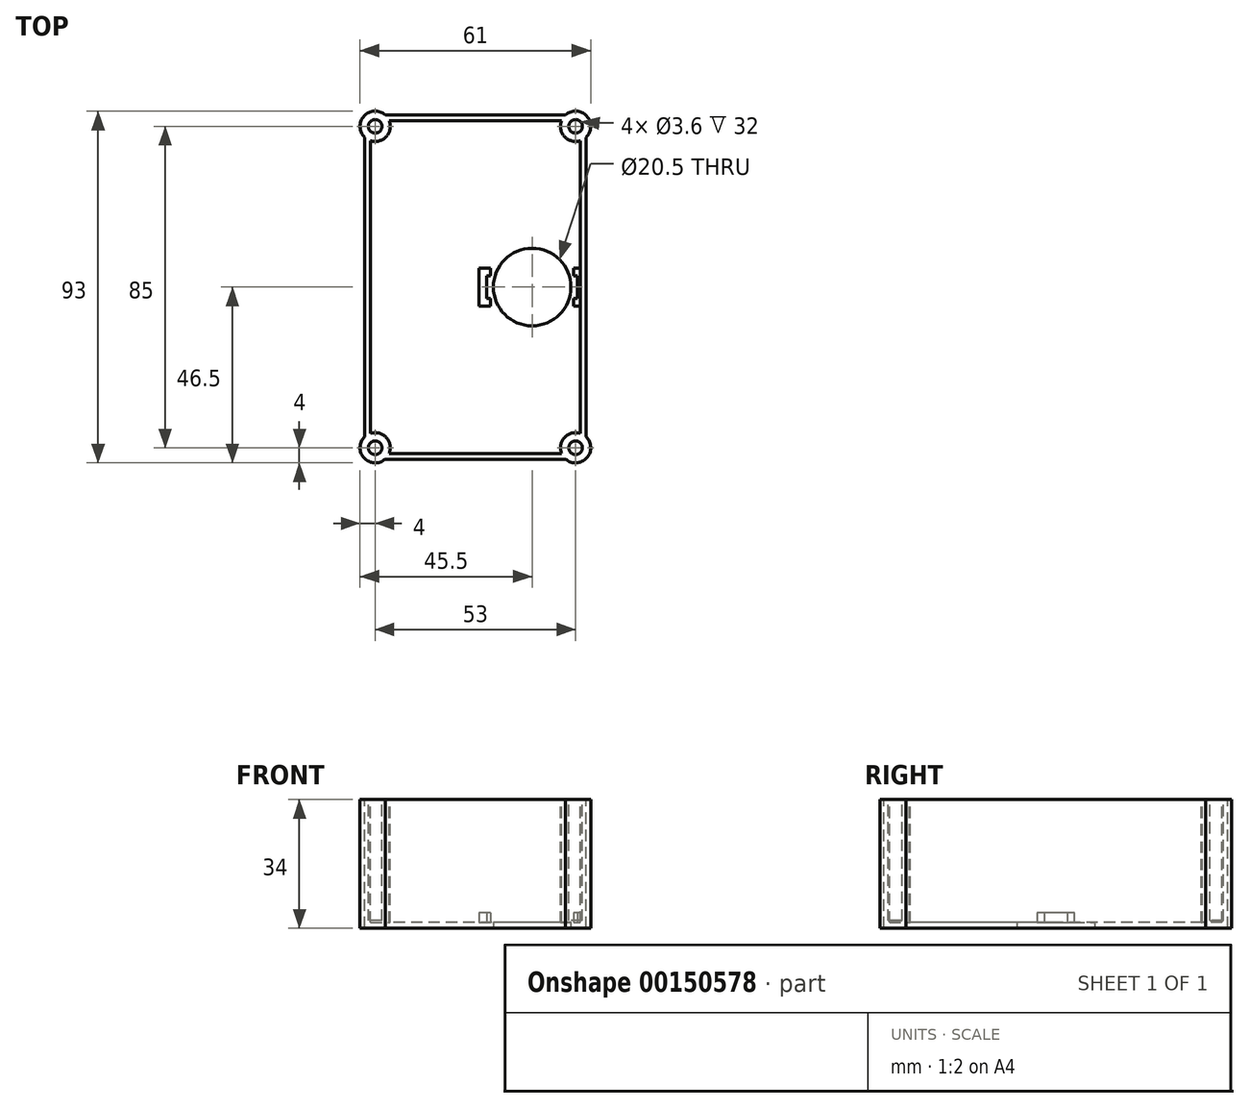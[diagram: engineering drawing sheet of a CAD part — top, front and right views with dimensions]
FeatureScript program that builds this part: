
annotation { "Feature Type Name" : "Feature", "Feature Type Description" : "" }
export const myFeature = defineFeature(function(context is Context, id is Id, definition is map)
    precondition{}
    {
        {
            var Q0;
            Q0=qCreatedBy(makeId("Top.planeOp"),FACE);
            var sketch = newSketch(context, id + "F0", { "sketchPlane" : qUnion([Q0])});
            skLineSegment(sketch, "E0.bottom", {"start": v(29.25, 45.5) * mm, "end": v(-29.25, 45.5) * mm});
            skLineSegment(sketch, "E0.top", {"start": v(29.25, -45.5) * mm, "end": v(-29.25, -45.5) * mm});
            skLineSegment(sketch, "E0.left", {"start": v(29.25, 45.5) * mm, "end": v(29.25, -45.5) * mm});
            skLineSegment(sketch, "E0.right", {"start": v(-29.25, 45.5) * mm, "end": v(-29.25, -45.5) * mm});
            skPoint(sketch, "E0.middle", {"position": v(0, 0) * mm});
            skSolve(sketch);
        }
        {
            var Q0;
            Q0=qSketchRegion(id+"F0",true);
            extrude(context, id + "F1", {"entities" : qUnion([Q0]), "oppositeDirection" : true, "depth" : 34 * mm});
        }
        {
            var Q0;
            Q0=makeQuery(id+"F1.opExtrude","CAP_FACE",FACE,{"disambiguationData":[OSD([sQuery(id+"F0.wireOp",EDGE,"E0.bottom"),sQuery(id+"F0.wireOp",EDGE,"E0.top"),sQuery(id+"F0.wireOp",EDGE,"E0.left"),sQuery(id+"F0.wireOp",EDGE,"E0.right")])],"isStart":true});
            shell(context, id + "F2", {"entities" : qUnion([Q0]), "thickness" : 1.5 * mm});
        }
        {
            var Q0;
            Q0=makeQuery(id+"F1.opExtrude","SWEPT_EDGE",EDGE,{"disambiguationData":[OSD([sQuery(id+"F0.wireOp",EDGE,"E0.bottom"),sQuery(id+"F0.wireOp",EDGE,"E0.right")])]});
            var Q1;
            Q1=makeQuery(id+"F1.opExtrude","SWEPT_EDGE",EDGE,{"disambiguationData":[OSD([sQuery(id+"F0.wireOp",EDGE,"E0.bottom"),sQuery(id+"F0.wireOp",EDGE,"E0.left")])]});
            var Q2;
            Q2=makeQuery(id+"F1.opExtrude","SWEPT_EDGE",EDGE,{"disambiguationData":[OSD([sQuery(id+"F0.wireOp",EDGE,"E0.top"),sQuery(id+"F0.wireOp",EDGE,"E0.right")])]});
            var Q3;
            Q3=makeQuery(id+"F1.opExtrude","SWEPT_EDGE",EDGE,{"disambiguationData":[OSD([sQuery(id+"F0.wireOp",EDGE,"E0.top"),sQuery(id+"F0.wireOp",EDGE,"E0.left")])]});
            fillet(context, id + "F3", {"entities" : qUnion([Q0, Q1, Q2, Q3]), "radius" : 3 * mm, "tangentPropagation" : true, "allowEdgeOverflow" : false});
        }
        {
            var Q0;
            Q0=makeQuery(id+"F2.opShell","OFFSET_EDGE",EDGE,{"disambiguationData":[OSD([sQuery(id+"F0.wireOp",EDGE,"E0.bottom"),sQuery(id+"F0.wireOp",EDGE,"E0.right")])]});
            var Q1;
            Q1=makeQuery(id+"F2.opShell","OFFSET_EDGE",EDGE,{"disambiguationData":[OSD([sQuery(id+"F0.wireOp",EDGE,"E0.top"),sQuery(id+"F0.wireOp",EDGE,"E0.right")])]});
            var Q2;
            Q2=makeQuery(id+"F2.opShell","OFFSET_EDGE",EDGE,{"disambiguationData":[OSD([sQuery(id+"F0.wireOp",EDGE,"E0.top"),sQuery(id+"F0.wireOp",EDGE,"E0.left")])]});
            var Q3;
            Q3=makeQuery(id+"F2.opShell","OFFSET_EDGE",EDGE,{"disambiguationData":[OSD([sQuery(id+"F0.wireOp",EDGE,"E0.bottom"),sQuery(id+"F0.wireOp",EDGE,"E0.left")])]});
            fillet(context, id + "F4", {"entities" : qUnion([Q0, Q1, Q2, Q3]), "radius" : 2 * mm, "tangentPropagation" : true, "allowEdgeOverflow" : false});
        }
        {
            var Q0;
            Q0=makeQuery(id+"F0.imprint","IMPRINT",FACE,{"disambiguationData":[TD([[makeQuery(id+"F0.imprint","IMPRINT",EDGE,{"derivedFrom":sQuery(id+"F0.wireOp",EDGE,"E0.bottom")}),1.0]])]});
            var sketch = newSketch(context, id + "F5", { "sketchPlane" : qUnion([Q0])});
            skLineSegment(sketch, "E1", {"start": v(26.5, -42.5) * mm, "end": v(26.5, 42.5) * mm, "construction": true});
            skLineSegment(sketch, "E2", {"start": v(-26.5, 42.5) * mm, "end": v(-26.5, -42.5) * mm, "construction": true});
            skLineSegment(sketch, "E3", {"start": v(26.5, -42.5) * mm, "end": v(-26.5, -42.5) * mm, "construction": true});
            skLineSegment(sketch, "E4", {"start": v(26.5, 42.5) * mm, "end": v(-26.5, 42.5) * mm, "construction": true});
            skCircle(sketch, "E5", {"center": v(26.5, -42.5) * mm, "radius": 4 * mm});
            skCircle(sketch, "E6", {"center": v(26.5, 42.5) * mm, "radius": 4 * mm});
            skCircle(sketch, "E7", {"center": v(-26.5, 42.5) * mm, "radius": 4 * mm});
            skCircle(sketch, "E8", {"center": v(-26.5, -42.5) * mm, "radius": 4 * mm});
            skSolve(sketch);
        }
        {
            var Q0;
            Q0=qSketchRegion(id+"F5",true);
            extrude(context, id + "F6", {"entities" : qUnion([Q0]), "operationType" : NewBodyOperationType.ADD, "oppositeDirection" : true, "depth" : 34 * mm});
        }
        {
            var Q0;
            Q0=qCreatedBy(makeId("Top.planeOp"),FACE);
            var sketch = newSketch(context, id + "F7", { "sketchPlane" : qUnion([Q0])});
            skCircle(sketch, "E9", {"center": v(26.5, -42.5) * mm, "radius": 1.8 * mm});
            skCircle(sketch, "E10", {"center": v(26.5, 42.5) * mm, "radius": 1.8 * mm});
            skCircle(sketch, "E11", {"center": v(-26.5, -42.5) * mm, "radius": 1.8 * mm});
            skCircle(sketch, "E12", {"center": v(-26.5, 42.5) * mm, "radius": 1.8 * mm});
            skSolve(sketch);
        }
        {
            var Q0;
            Q0=qSketchRegion(id+"F7",true);
            extrude(context, id + "F8", {"entities" : qUnion([Q0]), "operationType" : NewBodyOperationType.REMOVE, "oppositeDirection" : true, "depth" : 32 * mm});
        }
        {
            var Q0;
            Q0=makeQuery(id+"F0.imprint","IMPRINT",FACE,{"disambiguationData":[TD([[makeQuery(id+"F0.imprint","IMPRINT",EDGE,{"derivedFrom":sQuery(id+"F0.wireOp",EDGE,"E0.bottom")}),1.0]])]});
            var sketch = newSketch(context, id + "F9", { "sketchPlane" : qUnion([Q0])});
            skArc(sketch, "E13", {"start": v(27.75, -37.9) * mm, "mid": v(21.78, -38.03) * mm, "end": v(21.9, -44) * mm, "construction": true});
            skArc(sketch, "E14", {"start": v(21.9, 44) * mm, "mid": v(21.78, 38.03) * mm, "end": v(27.75, 37.9) * mm, "construction": true});
            skArc(sketch, "E15", {"start": v(-25.85, 35.82) * mm, "mid": v(-19.79, 37.94) * mm, "end": v(-21.9, 44) * mm, "construction": true});
            skArc(sketch, "E16", {"start": v(-21.9, -44) * mm, "mid": v(-22.32, -40.44) * mm, "end": v(-25.85, -39.82) * mm, "construction": true});
            skLineSegment(sketch, "E17", {"start": v(-25.85, -39.82) * mm, "end": v(-25.85, 35.82) * mm, "construction": true});
            skLineSegment(sketch, "E18", {"start": v(-21.9, 44) * mm, "end": v(21.9, 44) * mm, "construction": true});
            skLineSegment(sketch, "E19", {"start": v(27.75, -37.9) * mm, "end": v(27.75, 37.9) * mm, "construction": true});
            skLineSegment(sketch, "E20", {"start": v(21.9, -44) * mm, "end": v(-21.9, -44) * mm, "construction": true});
            skSolve(sketch);
        }
        {
            var Q0;
            Q0=makeQuery(id+"F6.boolean.opBoolean","MERGE",FACE,{"derivedFrom":[makeQuery(id+"F1.opExtrude","CAP_FACE",FACE,{"disambiguationData":[OSD([sQuery(id+"F0.wireOp",EDGE,"E0.bottom"),sQuery(id+"F0.wireOp",EDGE,"E0.top"),sQuery(id+"F0.wireOp",EDGE,"E0.left"),sQuery(id+"F0.wireOp",EDGE,"E0.right")])],"isStart":false}),makeQuery(id+"F6.opExtrude","CAP_FACE",FACE,{"disambiguationData":[OSD([sQuery(id+"F5.wireOp",EDGE,"E5")])],"isStart":false}),makeQuery(id+"F6.opExtrude","CAP_FACE",FACE,{"disambiguationData":[OSD([sQuery(id+"F5.wireOp",EDGE,"E6")])],"isStart":false}),makeQuery(id+"F6.opExtrude","CAP_FACE",FACE,{"disambiguationData":[OSD([sQuery(id+"F5.wireOp",EDGE,"E7")])],"isStart":false}),makeQuery(id+"F6.opExtrude","CAP_FACE",FACE,{"disambiguationData":[OSD([sQuery(id+"F5.wireOp",EDGE,"E8")])],"isStart":false})]});
            var sketch = newSketch(context, id + "F10", { "sketchPlane" : qUnion([Q0])});
            skLineSegment(sketch, "E21", {"start": v(0, 0) * mm, "end": v(15, 0) * mm, "construction": true});
            skCircle(sketch, "E22", {"center": v(15, 0) * mm, "radius": 10.25 * mm});
            skSolve(sketch);
        }
        {
            var Q0;
            Q0=makeQuery(id+"F1.opExtrude","CAP_FACE",FACE,{"disambiguationData":[OSD([sQuery(id+"F0.wireOp",EDGE,"E0.bottom"),sQuery(id+"F0.wireOp",EDGE,"E0.top"),sQuery(id+"F0.wireOp",EDGE,"E0.left"),sQuery(id+"F0.wireOp",EDGE,"E0.right")])],"isStart":false});
            var sketch = newSketch(context, id + "F11", { "sketchPlane" : qUnion([Q0])});
            skLineSegment(sketch, "E23", {"start": v(29, -5) * mm, "end": v(26, -5) * mm});
            skLineSegment(sketch, "E24", {"start": v(1, -5) * mm, "end": v(1, 5) * mm});
            skLineSegment(sketch, "E25", {"start": v(1, 5) * mm, "end": v(4, 5) * mm});
            skLineSegment(sketch, "E26", {"start": v(29, -5) * mm, "end": v(29, 5) * mm});
            skLineSegment(sketch, "E27", {"start": v(27, -3) * mm, "end": v(27, 3) * mm});
            skLineSegment(sketch, "E28", {"start": v(27, 3) * mm, "end": v(26, 3) * mm});
            skLineSegment(sketch, "E29", {"start": v(27, -3) * mm, "end": v(26, -3) * mm});
            skLineSegment(sketch, "E30", {"start": v(3, 3) * mm, "end": v(3, -3) * mm});
            skLineSegment(sketch, "E31", {"start": v(4, -5.7) * mm, "end": v(4, 6.3) * mm, "construction": true});
            skLineSegment(sketch, "E32", {"start": v(4, -5) * mm, "end": v(4, -3) * mm});
            skLineSegment(sketch, "E33", {"start": v(4, 3) * mm, "end": v(4, 5) * mm});
            skLineSegment(sketch, "E34", {"start": v(26, -6.46) * mm, "end": v(26, 5.94) * mm, "construction": true});
            skLineSegment(sketch, "E35", {"start": v(26, -5) * mm, "end": v(26, -3) * mm});
            skLineSegment(sketch, "E36", {"start": v(26, 3) * mm, "end": v(26, 5) * mm});
            skLineSegment(sketch, "E37.trimOffspring", {"start": v(4, -3) * mm, "end": v(3, -3) * mm});
            skLineSegment(sketch, "E38.trimOffspring", {"start": v(4, -5) * mm, "end": v(1, -5) * mm});
            skLineSegment(sketch, "E39.trimOffspring", {"start": v(4, 3) * mm, "end": v(3, 3) * mm});
            skLineSegment(sketch, "E40.trimOffspring", {"start": v(26, 5) * mm, "end": v(29, 5) * mm});
            skSolve(sketch);
        }
        {
            var Q0;
            Q0=qSketchRegion(id+"F11",true);
            extrude(context, id + "F12", {"entities" : qUnion([Q0]), "operationType" : NewBodyOperationType.ADD, "oppositeDirection" : true, "depth" : 4 * mm});
        }
        {
            var Q0;
            Q0=qSketchRegion(id+"F10",true);
            extrude(context, id + "F13", {"entities" : qUnion([Q0]), "operationType" : NewBodyOperationType.REMOVE, "oppositeDirection" : true, "depth" : 25 * mm});
        }
    });
